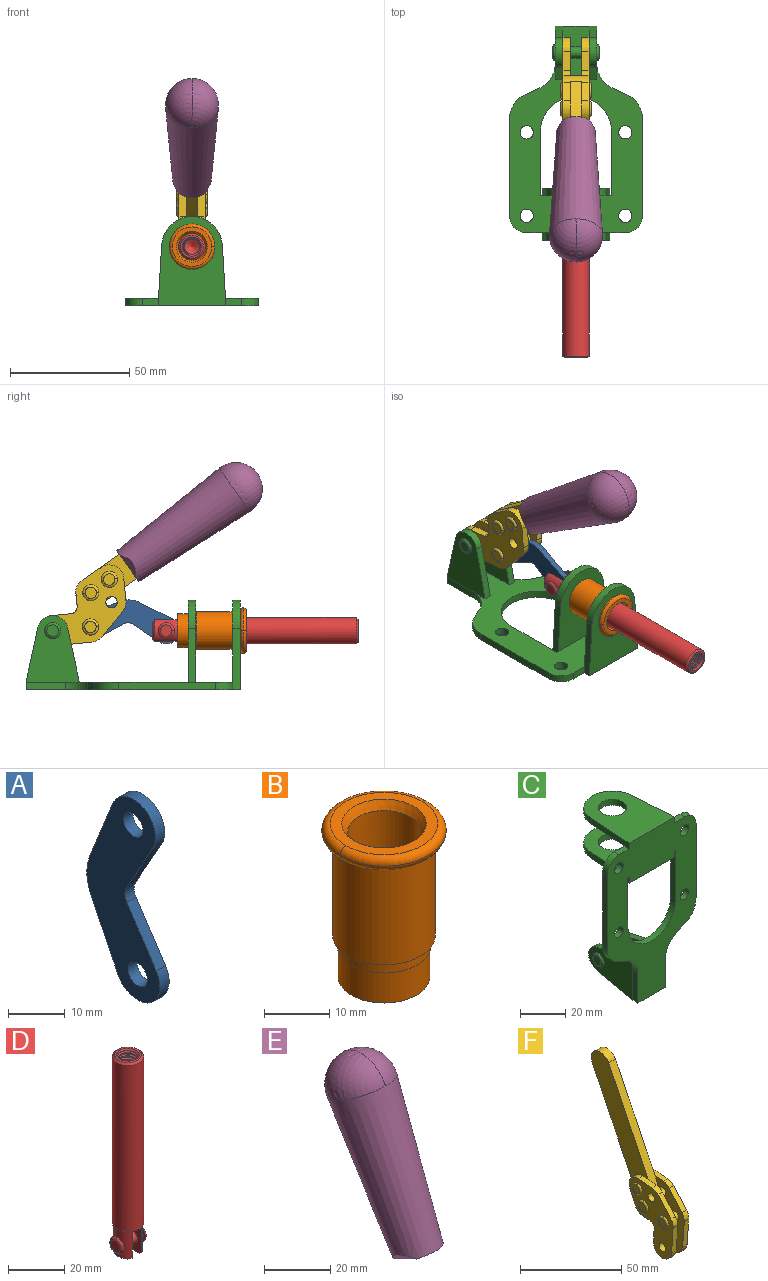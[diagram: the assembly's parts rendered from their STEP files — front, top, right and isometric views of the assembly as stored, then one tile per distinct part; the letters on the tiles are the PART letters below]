
ASSEMBLY  parts=6 mates=6
PART A: 12 faces, bbox 2.3x18.2x42.8 mm
  f0: cylinder r=2.4mm len=4.8mm, axis (1,0,0), area 34.9mm2, adj f4,f11
  f1: cylinder r=10.41mm len=8.47mm, axis (1,0,0), area 20.2mm2, adj f4,f9,f10,f11
  f2: cylinder r=3.05mm len=3.16mm, axis (1,0,0), area 7.7mm2, adj f4,f6,f7,f11
  f3: cylinder r=2.4mm len=4.8mm, axis (1,0,0), area 34.9mm2, adj f4,f11
  f4: plane 42.81x18.23mm, normal (-1,0,0), area 414.1mm2, adj f0,f1,f2,f3,f5,f6,f7,f8
  f5: cylinder r=5.54mm len=10.67mm, axis (1,0,0), area 41.8mm2, adj f4,f6,f10,f11
  f6: plane 11.66x6.53mm, normal (0,-0.87,-0.49), area 30.9mm2, adj f2,f4,f5,f11
  f7: plane 11.17x7.33mm, normal (0,-0.84,0.55), area 30.9mm2, adj f2,f4,f8,f11
  f8: cylinder r=5.54mm len=10.51mm, axis (1,0,0), area 41.8mm2, adj f4,f7,f9,f11
  f9: plane 13.67x6.67mm, normal (0,0.9,-0.44), area 35.1mm2, adj f1,f4,f8,f11
  f10: plane 14.1x5.7mm, normal (0,0.93,0.37), area 35.1mm2, adj f1,f4,f5,f11
  f11: plane 42.81x18.23mm, normal (1,0,0), area 414.1mm2, adj f0,f1,f2,f3,f5,f6,f7,f8
PART B: 15 faces, bbox 20.6x20.6x28.7 mm
  f0: torus R=8.26mm, axis (0,0,1), area 56.8mm2, adj f1,f10,f12
  f1: torus R=8.26mm, axis (0,0,1), area 56.8mm2, adj f0,f6,f13
  f2: cylinder r=5.59mm len=25.91mm, axis (0,0,1), area 909.6mm2, adj f3,f4
  f3: cone r=6.86mm half-angle=45deg, axis (0,0,-1), area 70.2mm2, adj f2,f14
  f4: cone r=6.47mm half-angle=30deg, axis (0,0,1), area 66.7mm2, adj f2,f13
  f5: cylinder r=7.04mm len=14.07mm, axis (0,0,1), area 252.6mm2, adj f11,f14
  f6: torus R=8.26mm, axis (0,0,1), area 56.8mm2, adj f1,f12,f13
  f7: cylinder r=7.16mm len=14.33mm, axis (0,0,1), area 91.5mm2, adj f9,f11
  f8: cylinder r=7.86mm len=18.42mm, axis (0,0,1), area 909.6mm2, adj f9,f10
  f9: plane 15.72x15.72mm, normal (0,0,-1), area 33mm2, adj f7,f8
  f10: plane 16.51x16.51mm, normal (0,0,-1), area 19.9mm2, adj f0,f8,f12
  f11: plane 14.33x14.33mm, normal (0,0,-1), area 5.7mm2, adj f5,f7
  f12: torus R=8.26mm, axis (0,0,1), area 56.8mm2, adj f0,f6,f10
  f13: plane 16.51x16.51mm, normal (0,0,1), area 82.7mm2, adj f1,f4,f6
  f14: plane 14.07x14.07mm, normal (0,0,-1), area 7.8mm2, adj f3,f5
PART C: 55 faces, bbox 55.7x37.4x89.8 mm
  f0: torus R=2.41mm, axis (-1,0,0), area 15mm2, adj f11,f15,f25
  f1: torus R=2.41mm, axis (-1,0,0), area 15mm2, adj f10,f12,f22
  f2: cylinder r=2.78mm len=5.56mm, axis (0,-1,0), area 54.2mm2, adj f30,f54
  f3: cylinder r=14.99mm len=29.97mm, axis (0,-1,0), area 145.9mm2, adj f30,f49,f53,f54
  f4: cylinder r=2.78mm len=5.56mm, axis (0,-1,0), area 54.2mm2, adj f30,f54
  f5: cylinder r=2.78mm len=5.56mm, axis (0,-1,0), area 54.2mm2, adj f30,f54
  f6: cylinder r=2.78mm len=5.56mm, axis (0,-1,0), area 54.2mm2, adj f30,f54
  f7: cylinder r=6.35mm len=12.7mm, axis (0,0,1), area 123.6mm2, adj f27,f51
  f8: cylinder r=6.35mm len=12.7mm, axis (0,0,-1), area 124.7mm2, adj f21,f35
  f9: cylinder r=2.41mm len=11.18mm, axis (-1,0,0), area 169.4mm2, adj f16,f19
  f10: plane 4.83x4.83mm, normal (1,0,0), area 18.3mm2, adj f1,f12
  f11: plane 4.83x4.83mm, normal (-1,0,0), area 18.3mm2, adj f0,f15
  f12: torus R=2.41mm, axis (-1,0,0), area 15mm2, adj f1,f10,f22
  f13: cylinder r=6.35mm len=12.41mm, axis (1,0,0), area 53.4mm2, adj f18,f19,f22,f23
  f14: cylinder r=6.35mm len=12.41mm, axis (-1,0,0), area 53.4mm2, adj f16,f17,f24,f25
  f15: torus R=2.41mm, axis (-1,0,0), area 15mm2, adj f0,f11,f25
  f16: plane 27.86x22.35mm, normal (1,0,0), area 425.4mm2, adj f9,f14,f17,f24,f30
  f17: plane 22.86x4.97mm, normal (0,0.21,0.98), area 72.5mm2, adj f14,f16,f25,f30
  f18: plane 22.86x4.97mm, normal (0,0.21,0.98), area 72.5mm2, adj f13,f19,f22,f30
  f19: plane 27.86x22.35mm, normal (-1,0,0), area 425.4mm2, adj f9,f13,f18,f23,f30
  f20: cylinder r=12.7mm len=25.35mm, axis (0,0,-1), area 119.8mm2, adj f21,f34,f35,f36
  f21: plane 34.21x28.07mm, normal (0,0,-1), area 702.4mm2, adj f8,f20,f30,f34,f36
  f22: plane 27.96x22.45mm, normal (1,0,0), area 407.2mm2, adj f1,f12,f13,f18,f23,f30,f42,f43
  f23: plane 22.86x4.97mm, normal (0,0.21,-0.98), area 72.5mm2, adj f13,f19,f22,f44
  f24: plane 22.86x4.97mm, normal (0,0.21,-0.98), area 72.5mm2, adj f14,f16,f25,f44
  f25: plane 27.86x22.35mm, normal (-1,0,0), area 407.1mm2, adj f0,f14,f15,f17,f24,f30,f45,f46
  f26: plane 3.1x0.95mm, normal (0,0,-1), area 2.7mm2, adj f30,f49,f50,f54
  f27: plane 34.21x28.07mm, normal (0,0,1), area 702.4mm2, adj f7,f28,f30,f50,f52
  f28: cylinder r=12.7mm len=25.35mm, axis (0,0,1), area 118.8mm2, adj f27,f50,f51,f52
  f29: plane 3.1x0.95mm, normal (0,0,-1), area 2.7mm2, adj f30,f52,f53,f54
  f30: plane 86.54x55.63mm, normal (0,1,0), area 2362.9mm2, adj f2,f3,f4,f5,f6,f16,f17,f18
  f31: plane 40.56x3.1mm, normal (-1,0,0), area 125.7mm2, adj f30,f32,f48,f54
  f32: cylinder r=7.11mm len=7.11mm, axis (0,-1,0), area 34.6mm2, adj f30,f31,f33,f54
  f33: plane 6.67x3.1mm, normal (0,0,1), area 20.4mm2, adj f30,f32,f34,f54
  f34: plane 25.39x3.13mm, normal (-1,0.06,0), area 79.5mm2, adj f20,f21,f33,f35,f54
  f35: plane 37.31x28.45mm, normal (0,0,1), area 789.9mm2, adj f8,f20,f34,f36,f54
  f36: plane 25.39x3.13mm, normal (1,0.06,0), area 79.5mm2, adj f20,f21,f35,f37,f54
  f37: plane 6.67x3.1mm, normal (0,0,1), area 20.4mm2, adj f30,f36,f38,f54
  f38: cylinder r=7.11mm len=7.11mm, axis (0,-1,0), area 34.6mm2, adj f30,f37,f39,f54
  f39: plane 40.56x3.1mm, normal (1,0,0), area 125.7mm2, adj f30,f38,f40,f54
  f40: cylinder r=11.18mm len=10.16mm, axis (0,-1,0), area 39.5mm2, adj f30,f39,f41,f54
  f41: plane 6.09x3.1mm, normal (0.42,0,-0.91), area 20.8mm2, adj f30,f40,f42,f54
  f42: cylinder r=11.18mm len=9.41mm, axis (0,-1,0), area 37.2mm2, adj f22,f30,f41,f43,f54
  f43: plane 16.5x3.1mm, normal (1,0,0), area 51.1mm2, adj f22,f42,f44,f54
  f44: plane 17.37x3.1mm, normal (0,0,-1), area 53.8mm2, adj f23,f24,f30,f43,f45,f54
  f45: plane 16.5x3.1mm, normal (-1,0,0), area 51.1mm2, adj f25,f44,f46,f54
  f46: cylinder r=11.18mm len=9.41mm, axis (0,-1,0), area 37.2mm2, adj f25,f30,f45,f47,f54
  f47: plane 6.09x3.1mm, normal (-0.42,0,-0.91), area 20.8mm2, adj f30,f46,f48,f54
  f48: cylinder r=11.18mm len=10.16mm, axis (0,-1,0), area 39.5mm2, adj f30,f31,f47,f54
  f49: plane 26.54x3.1mm, normal (-1,0,0), area 82.3mm2, adj f3,f26,f30,f54
  f50: plane 25.39x3.1mm, normal (1,0.06,0), area 78.8mm2, adj f26,f27,f28,f51,f54
  f51: plane 37.31x28.45mm, normal (0,0,-1), area 789.9mm2, adj f7,f28,f50,f52,f54
  f52: plane 25.39x3.1mm, normal (-1,0.06,0), area 78.8mm2, adj f27,f28,f29,f51,f54
  f53: plane 26.54x3.1mm, normal (1,0,0), area 82.3mm2, adj f3,f29,f30,f54
  f54: plane 89.66x55.63mm, normal (0,-1,0), area 2678.5mm2, adj f2,f3,f4,f5,f6,f26,f29,f31
PART D: 48 faces, bbox 12.6x11.1x86.1 mm
  f0: torus R=2.41mm, axis (-1,0,0), area 15mm2, adj f30,f32,f34
  f1: torus R=2.41mm, axis (-1,0,0), area 15mm2, adj f29,f31,f33
  f2: cylinder r=5.54mm len=72.39mm, axis (0,0,1), area 2518.5mm2, adj f3,f4,f42,f43
  f3: cone r=5.54mm half-angle=45deg, axis (0,0,1), area 7.6mm2, adj f2,f5,f41
  f4: cone r=5.54mm half-angle=45deg, axis (0,0,-1), area 34.9mm2, adj f2,f39
  f5: cylinder r=5.08mm len=11.48mm, axis (0,0,1), area 108.3mm2, adj f3,f7,f8,f41
  f6: cylinder r=2.41mm len=4.83mm, axis (-1,0,0), area 71.2mm2, adj f40,f41
  f7: cylinder r=2.41mm len=4.83mm, axis (-1,0,0), area 7.6mm2, adj f5,f34
  f8: cone r=5.08mm half-angle=45deg, axis (0,0,1), area 10.6mm2, adj f5,f37,f41
  f9: cone r=3.98mm half-angle=45deg, axis (0,0,1), area 17.6mm2, adj f27,f39,f45,f46,f47
  f10: cylinder r=2.41mm len=4.83mm, axis (-1,0,0), area 7.6mm2, adj f33,f38
  f11: cylinder r=3.2mm len=6.4mm, axis (0,0,1), area 78.4mm2, adj f12,f28,f44,f45,f47
  f12: cylinder r=3.2mm len=6.4mm, axis (0,0,1), area 10.5mm2, adj f11,f13,f45,f47
  f13: cylinder r=3.2mm len=6.4mm, axis (0,0,1), area 10.5mm2, adj f12,f14,f45,f47
  f14: cylinder r=3.2mm len=6.4mm, axis (0,0,1), area 10.5mm2, adj f13,f15,f45,f47
  f15: cylinder r=3.2mm len=6.4mm, axis (0,0,1), area 10.5mm2, adj f14,f16,f45,f47
  f16: cylinder r=3.2mm len=6.4mm, axis (0,0,1), area 10.5mm2, adj f15,f17,f45,f47
  f17: cylinder r=3.2mm len=6.4mm, axis (0,0,1), area 10.5mm2, adj f16,f18,f45,f47
  f18: cylinder r=3.2mm len=6.4mm, axis (0,0,1), area 10.5mm2, adj f17,f19,f45,f47
  f19: cylinder r=3.2mm len=6.4mm, axis (0,0,1), area 10.5mm2, adj f18,f20,f45,f47
  f20: cylinder r=3.2mm len=6.4mm, axis (0,0,1), area 10.5mm2, adj f19,f21,f45,f47
  f21: cylinder r=3.2mm len=6.4mm, axis (0,0,1), area 10.5mm2, adj f20,f22,f45,f47
  f22: cylinder r=3.2mm len=6.4mm, axis (0,0,1), area 10.5mm2, adj f21,f23,f45,f47
  f23: cylinder r=3.2mm len=6.4mm, axis (0,0,1), area 10.5mm2, adj f22,f24,f45,f47
  f24: cylinder r=3.2mm len=6.4mm, axis (0,0,1), area 10.5mm2, adj f23,f25,f45,f47
  f25: cylinder r=3.2mm len=6.4mm, axis (0,0,1), area 10.5mm2, adj f24,f26,f45,f47
  f26: cylinder r=3.2mm len=6.4mm, axis (0,0,1), area 10.5mm2, adj f25,f27,f45,f47
  f27: cylinder r=3.2mm len=6.4mm, axis (0,0,1), area 7.4mm2, adj f9,f26,f45,f47
  f28: cone r=3.2mm half-angle=60deg, axis (0,0,1), area 37.2mm2, adj f11
  f29: plane 4.83x4.83mm, normal (-1,0,0), area 18.3mm2, adj f1,f31
  f30: plane 4.83x4.83mm, normal (1,0,0), area 18.3mm2, adj f0,f32
  f31: torus R=2.41mm, axis (-1,0,0), area 15mm2, adj f1,f29,f33
  f32: torus R=2.41mm, axis (-1,0,0), area 15mm2, adj f0,f30,f34
  f33: plane 6.83x6.83mm, normal (1,0,0), area 18.3mm2, adj f1,f10,f31
  f34: plane 6.83x6.83mm, normal (-1,0,0), area 18.3mm2, adj f0,f7,f32
  f35: cone r=5.08mm half-angle=45deg, axis (0,0,1), area 10.6mm2, adj f36,f38,f40
  f36: plane 7.25x1.97mm, normal (0,0,-1), area 10mm2, adj f35,f40
  f37: plane 7.25x1.97mm, normal (0,0,-1), area 10mm2, adj f8,f41
  f38: cylinder r=5.08mm len=11.48mm, axis (0,0,1), area 108.3mm2, adj f10,f35,f40,f42
  f39: plane 9.55x9.55mm, normal (0,0,1), area 22mm2, adj f4,f9
  f40: plane 12.76x10.09mm, normal (1,0,0), area 95.7mm2, adj f6,f35,f36,f38,f42,f43
  f41: plane 12.76x10.09mm, normal (-1,0,0), area 95.7mm2, adj f3,f5,f6,f8,f37,f43
  f42: cone r=5.54mm half-angle=45deg, axis (0,0,1), area 7.6mm2, adj f2,f38,f40
  f43: plane 11.07x4.7mm, normal (0,0,-1), area 50.4mm2, adj f2,f40,f41
  f44: plane 0.89x0.62mm, normal (-1,0,0), area 0.3mm2, adj f11,f45,f46,f47
  f45: bspline ~24.8x7.63mm, area 266.6mm2, adj f9,f11,f12,f13,f14,f15,f16,f17
  f46: bspline ~24.87x7.63mm, area 73.6mm2, adj f9,f44,f45,f47
  f47: bspline ~24.98x7.63mm, area 272.5mm2, adj f9,f11,f12,f13,f14,f15,f16,f17
PART E: 11 faces, bbox 22.3x42.6x64.5 mm
  f0: sphere r=11.13mm, area 411.4mm2, adj f1,f8
  f1: cone r=11.11mm half-angle=3.3deg, axis (0,0.44,0.9), area 3251.8mm2, adj f0,f7,f8,f9,f10
  f2: cylinder r=6.16mm len=11.7mm, axis (1,0,0), area 89.5mm2, adj f3,f4,f5,f6
  f3: plane 60.23x36.75mm, normal (-1,0,0), area 763.6mm2, adj f2,f4,f6,f10
  f4: plane 51.37x25.05mm, normal (0,0.9,-0.44), area 264.2mm2, adj f2,f3,f5,f10
  f5: plane 60.23x36.75mm, normal (1,0,0), area 763.6mm2, adj f2,f4,f6,f10
  f6: plane 51.37x25.05mm, normal (0,-0.9,0.44), area 264.2mm2, adj f2,f3,f5,f10
  f7: plane 9.95x5.95mm, normal (0.71,-0.31,-0.64), area 25.8mm2, adj f1,f10
  f8: sphere r=11.13mm, area 411.4mm2, adj f0,f1
  f9: plane 9.95x5.95mm, normal (-0.71,-0.31,-0.64), area 25.8mm2, adj f1,f10
  f10: plane 14.27x11.38mm, normal (0,-0.44,-0.9), area 106.7mm2, adj f1,f3,f4,f5,f6,f7,f9
PART F: 59 faces, bbox 12.9x60.2x99.6 mm
  f0: torus R=2.39mm, axis (-1,0,0), area 14.9mm2, adj f20,f43,f51
  f1: torus R=2.39mm, axis (-1,0,0), area 14.9mm2, adj f19,f42,f51
  f2: torus R=2.39mm, axis (-1,0,0), area 14.9mm2, adj f18,f35,f51
  f3: torus R=2.39mm, axis (-1,0,0), area 14.9mm2, adj f14,f17,f23
  f4: torus R=2.39mm, axis (-1,0,0), area 14.9mm2, adj f13,f16,f23
  f5: torus R=2.39mm, axis (-1,0,0), area 14.9mm2, adj f12,f15,f23
  f6: cylinder r=2.39mm len=4.78mm, axis (1,0,0), area 46.5mm2, adj f48,f50,f51
  f7: cylinder r=2.39mm len=4.78mm, axis (1,0,0), area 46.5mm2, adj f50,f51
  f8: cylinder r=6.35mm len=12.68mm, axis (1,0,0), area 61.8mm2, adj f38,f39,f50,f51
  f9: cylinder r=2.39mm len=4.78mm, axis (-1,0,0), area 70.5mm2, adj f46,f50
  f10: cylinder r=2.39mm len=4.78mm, axis (-1,0,0), area 46.5mm2, adj f23,f45,f46
  f11: cylinder r=2.39mm len=4.78mm, axis (-1,0,0), area 46.5mm2, adj f23,f46
  f12: plane 4.78x4.78mm, normal (1,0,0), area 17.9mm2, adj f5,f15
  f13: plane 4.78x4.78mm, normal (1,0,0), area 17.9mm2, adj f4,f16
  f14: plane 4.78x4.78mm, normal (1,0,0), area 17.9mm2, adj f3,f17
  f15: torus R=2.39mm, axis (-1,0,0), area 14.9mm2, adj f5,f12,f23
  f16: torus R=2.39mm, axis (-1,0,0), area 14.9mm2, adj f4,f13,f23
  f17: torus R=2.39mm, axis (-1,0,0), area 14.9mm2, adj f3,f14,f23
  f18: plane 4.78x4.78mm, normal (-1,0,0), area 17.9mm2, adj f2,f35
  f19: plane 4.78x4.78mm, normal (-1,0,0), area 17.9mm2, adj f1,f42
  f20: plane 4.78x4.78mm, normal (-1,0,0), area 17.9mm2, adj f0,f43
  f21: plane 2.26x0.2mm, normal (1,0,0), area 0.2mm2, adj f31,f44
  f22: plane 2.26x0.2mm, normal (-1,0,0), area 0.2mm2, adj f41,f44
  f23: plane 39.37x30.77mm, normal (1,0,0), area 565.5mm2, adj f3,f4,f5,f10,f11,f15,f16,f17
  f24: cylinder r=6.1mm len=4.15mm, axis (-1,0,0), area 14.7mm2, adj f23,f25,f32,f46
  f25: plane 10.25x9.01mm, normal (0,-0.75,0.66), area 42.3mm2, adj f23,f24,f26,f46
  f26: cylinder r=6.35mm len=4.64mm, axis (-1,0,0), area 15.6mm2, adj f23,f25,f27,f46
  f27: plane 15.84x3.1mm, normal (0,-1,-0.07), area 49.2mm2, adj f23,f26,f28,f46
  f28: cylinder r=6.35mm len=12.68mm, axis (-1,0,0), area 61.8mm2, adj f23,f27,f29,f46
  f29: plane 8.11x3.1mm, normal (0,1,0.07), area 25.2mm2, adj f23,f28,f30,f46
  f30: cylinder r=3.05mm len=3.25mm, axis (-1,0,0), area 14.8mm2, adj f23,f29,f31,f46
  f31: plane 5.99x3.1mm, normal (0,0.07,-1), area 18.6mm2, adj f21,f23,f30,f44,f46
  f32: plane 9.5x3.1mm, normal (0,-0.07,1), area 29.5mm2, adj f23,f24,f33,f46,f47
  f33: cylinder r=6.1mm len=8.63mm, axis (-1,0,0), area 39.1mm2, adj f23,f32,f34,f47
  f34: plane 8.65x3.96mm, normal (0,0.91,-0.42), area 29.5mm2, adj f23,f33,f44,f47
  f35: torus R=2.39mm, axis (-1,0,0), area 14.9mm2, adj f2,f18,f51
  f36: plane 10.25x9.01mm, normal (0,-0.75,0.66), area 42.3mm2, adj f37,f49,f50,f51
  f37: cylinder r=6.35mm len=4.64mm, axis (1,0,0), area 15.6mm2, adj f36,f38,f50,f51
  f38: plane 15.84x3.1mm, normal (0,-1,-0.07), area 49.2mm2, adj f8,f37,f50,f51
  f39: plane 8.11x3.1mm, normal (0,1,0.07), area 25.2mm2, adj f8,f40,f50,f51
  f40: cylinder r=3.05mm len=3.25mm, axis (1,0,0), area 14.8mm2, adj f39,f41,f50,f51
  f41: plane 5.99x3.1mm, normal (0,0.07,-1), area 18.6mm2, adj f22,f40,f44,f50,f51
  f42: torus R=2.39mm, axis (-1,0,0), area 14.9mm2, adj f1,f19,f51
  f43: torus R=2.39mm, axis (-1,0,0), area 14.9mm2, adj f0,f20,f51
  f44: cylinder r=6.35mm len=12.12mm, axis (-1,0,0), area 128.9mm2, adj f21,f22,f23,f31,f34,f41,f46,f47
  f45: plane 2.65x1.35mm, normal (1,0,0), area 1mm2, adj f10,f55
  f46: plane 39.08x20.42mm, normal (-1,0,0), area 412.5mm2, adj f9,f10,f11,f24,f25,f26,f27,f28
  f47: plane 77.62x39.82mm, normal (1,0,0), area 850mm2, adj f32,f33,f34,f44,f53,f54,f55
  f48: plane 2.65x1.35mm, normal (-1,0,0), area 1mm2, adj f6,f55
  f49: cylinder r=6.1mm len=4.15mm, axis (1,0,0), area 14.7mm2, adj f36,f50,f51,f56
  f50: plane 39.08x20.42mm, normal (1,0,0), area 412.5mm2, adj f6,f7,f8,f9,f36,f37,f38,f39
  f51: plane 39.37x30.77mm, normal (-1,0,0), area 565.5mm2, adj f0,f1,f2,f6,f7,f8,f35,f36
  f52: plane 8.65x3.96mm, normal (0,0.91,-0.42), area 29.5mm2, adj f44,f51,f57,f58
  f53: plane 68.49x33.4mm, normal (0,0.9,-0.44), area 358.1mm2, adj f44,f47,f54,f58
  f54: cylinder r=6.35mm len=12.06mm, axis (1,0,0), area 93.7mm2, adj f47,f53,f55,f58
  f55: plane 68.49x33.4mm, normal (0,-0.9,0.44), area 358.1mm2, adj f44,f45,f46,f47,f48,f50,f54,f58
  f56: plane 9.5x3.1mm, normal (0,-0.07,1), area 29.5mm2, adj f49,f50,f51,f57,f58
  f57: cylinder r=6.1mm len=8.63mm, axis (1,0,0), area 39.1mm2, adj f51,f52,f56,f58
  f58: plane 77.62x39.82mm, normal (-1,0,0), area 850mm2, adj f44,f52,f53,f54,f55,f56,f57
PLACE A rot(axis=(0,-0.7,-0.71),180deg) t=(0,10.3,1.33)mm
PLACE B rot(axis=(1,0,0),90deg) t=(0,9.14,0)mm
PLACE C rot(axis=(1,0,0),90deg) t=(0,9.14,0)mm fixed
PLACE D rot(axis=(1,0,0),90deg) t=(0,9.19,0)mm
PLACE E rot(axis=(1,0,0),80.4deg) t=(0,5.49,5.68)mm
PLACE F rot(axis=(1,0,0),80.4deg) t=(0,5.49,5.68)mm
MATE revolute A.f3 <-> D.f6  axis (-1,0,0) through (0,-6.28,24.61)mm
MATE fastened B.f0 <-> C.f7  axis (0,1,0) through (0,-37.25,24.61)mm
MATE fastened F.f54 <-> E.f2  axis (1,0,0) through (0,-36.71,84.84)mm
MATE slider D.f2 <-> B.f12  axis (0,-1,0) through (0,-49.59,24.61)mm
MATE revolute A.f5 <-> F.f4  axis (-1,0,0) through (0,25.43,26.15)mm
MATE revolute F.f7 <-> C.f0  axis (-1,0,0) through (0,41.23,24.61)mm
